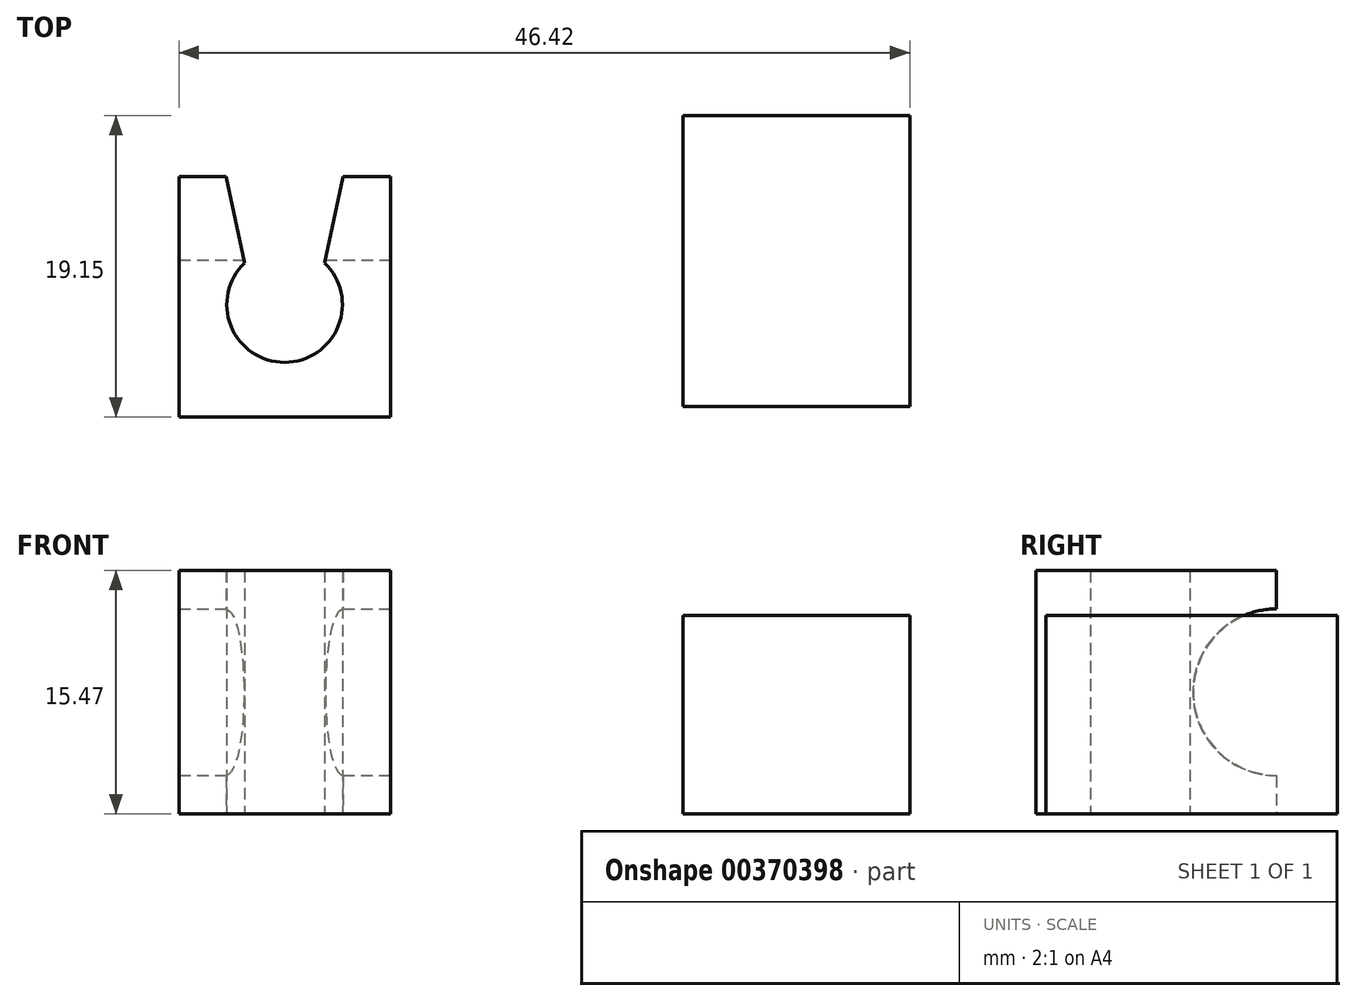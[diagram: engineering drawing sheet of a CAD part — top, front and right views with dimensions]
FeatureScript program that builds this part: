
annotation { "Feature Type Name" : "Feature", "Feature Type Description" : "" }
export const myFeature = defineFeature(function(context is Context, id is Id, definition is map)
    precondition{}
    {
        {
            var Q0;
            Q0=qCreatedBy(makeId("Top.planeOp"),FACE);
            var sketch = newSketch(context, id + "F0", { "sketchPlane" : qUnion([Q0])});
            skLineSegment(sketch, "E0.bottom", {"start": v(-15.68, -3.88) * mm, "end": v(-12.67, -3.88) * mm});
            skLineSegment(sketch, "E0.top", {"start": v(-15.68, -19.15) * mm, "end": v(-2.25, -19.15) * mm});
            skLineSegment(sketch, "E0.left", {"start": v(-15.68, -3.88) * mm, "end": v(-15.68, -19.15) * mm});
            skLineSegment(sketch, "E0.right", {"start": v(-2.25, -3.88) * mm, "end": v(-2.25, -19.15) * mm});
            skArc(sketch, "E1", {"start": v(-11.5, -9.36) * mm, "mid": v(-8.97, -15.68) * mm, "end": v(-6.43, -9.36) * mm});
            skLineSegment(sketch, "E2", {"start": v(-2.25, -3.88) * mm, "end": v(-5.26, -3.88) * mm});
            skLineSegment(sketch, "E3", {"start": v(-5.26, -3.88) * mm, "end": v(-6.43, -9.36) * mm});
            skLineSegment(sketch, "E4", {"start": v(-12.67, -3.88) * mm, "end": v(-11.5, -9.36) * mm});
            skLineSegment(sketch, "E5.trimOffspring", {"start": v(-5.26, -3.88) * mm, "end": v(-2.25, -3.88) * mm});
            skSolve(sketch);
        }
        {
            var Q0;
            Q0=makeQuery(id+"F0.imprint","IMPRINT",FACE,{"disambiguationData":[TD([[makeQuery(id+"F0.imprint","IMPRINT",EDGE,{"derivedFrom":sQuery(id+"F0.wireOp",EDGE,"E0.top")}),1.0]])]});
            extrude(context, id + "F1", {"entities" : qUnion([Q0]), "depth" : 15.47 * mm});
        }
        {
            var Q0;
            Q0=makeQuery(id+"F1.opExtrude","SWEPT_FACE",FACE,{"disambiguationData":[OSD([sQuery(id+"F0.wireOp",EDGE,"E0.right")])]});
            var sketch = newSketch(context, id + "F2", { "sketchPlane" : qUnion([Q0])});
            skLineSegment(sketch, "E6", {"start": v(-3.88, 15.47) * mm, "end": v(-3.88, 13.03) * mm});
            skLineSegment(sketch, "E7", {"start": v(-3.88, 0) * mm, "end": v(-3.88, 2.46) * mm});
            skLineSegment(sketch, "E8", {"start": v(-3.88, 7.73) * mm, "end": v(-9.12, 7.73) * mm});
            skPoint(sketch, "E8.endSnap0", {"position": v(-3.88, 7.73) * mm});
            skCircle(sketch, "E9", {"center": v(-3.88, 7.73) * mm, "radius": 5.3 * mm});
            skSolve(sketch);
        }
        {
            var Q0;
            {var subQ0=sQuery(id+"F2.wireOp",EDGE,"E7");var subQ3=sQuery(id+"F2.wireOp",EDGE,"E9");var subQ4=makeQuery(id+"F2.imprint","INTERSECT",VERTEX,{"derivedFrom":[subQ0,subQ3]});Q0=makeQuery(id+"F2.imprint","IMPRINT",FACE,{"disambiguationData":[TD([[makeQuery(id+"F2.imprint","IMPRINT",EDGE,{"disambiguationData":[TD([[subQ4,1.0]])],"derivedFrom":subQ0}),-1.0]])]});}
            extrude(context, id + "F3", {"entities" : qUnion([Q0]), "operationType" : NewBodyOperationType.REMOVE, "oppositeDirection" : true, "depth" : 25.4 * mm});
        }
        {
            var Q0;
            Q0=qCreatedBy(makeId("Top.planeOp"),FACE);
            var sketch = newSketch(context, id + "F4", { "sketchPlane" : qUnion([Q0])});
            skLineSegment(sketch, "E10.bottom", {"start": v(16.34, 0) * mm, "end": v(30.74, 0) * mm});
            skLineSegment(sketch, "E10.top", {"start": v(16.34, -18.5) * mm, "end": v(30.74, -18.5) * mm});
            skLineSegment(sketch, "E10.left", {"start": v(16.34, 0) * mm, "end": v(16.34, -18.5) * mm});
            skLineSegment(sketch, "E10.right", {"start": v(30.74, 0) * mm, "end": v(30.74, -18.5) * mm});
            skSolve(sketch);
        }
        {
            var Q0;
            Q0=makeQuery(id+"F4.imprint","IMPRINT",FACE,{"disambiguationData":[TD([[makeQuery(id+"F4.imprint","IMPRINT",EDGE,{"derivedFrom":sQuery(id+"F4.wireOp",EDGE,"E10.bottom")}),-1.0]])]});
            extrude(context, id + "F5", {"entities" : qUnion([Q0]), "depth" : 12.6 * mm});
        }
    });
